# Revit family: Gleiter GL-100 m.Lasche, 2xAG
name_source: partatom
category: HLS-Bauteile
revit_build: Autodesk Revit 2017 (Build: 20190507_1515(x64)
units: mm (PartAtom-declared; Revit-internal decimal feet)

## family parameters
Arbeitsebenenbasiert = Ja
Beim Laden mit Abzugskörper schneiden = Nein
Bemaßung runder Anschluss = Durchmesser verwenden
Gemeinsam genutzt = Ja
Immer vertikal = Nein
Raumberechnungspunkt = Nein
Teiletyp = Normal

## types (4) — shared parameters
Anzahl Anschlüsse = 2
Ausführung = mit Lasche
B = 160 mm  [stored 0.524934 ft]
B1 = 50 mm  [stored 0.164042 ft]
Breite = 125 mm  [stored 0.410105 ft]
DVS = 14 mm  [stored 0.0459318 ft]
Fabrikat = MEFA
Firma = MEFA Befestigungs- und Montagesysteme GmbH
Gleitreibungsfaktor = 0.15 - 0.25
Haftreibungsfaktor = 0,2 - 0,3
Kurztext1 = Gleiter axial GL 100
L = 125 mm  [stored 0.410105 ft]
L1 = 96 mm  [stored 0.314961 ft]
Lochdurchmesser = 13 mm
Länge = 160 mm  [stored 0.524934 ft]
Material Gleitelement = Stahl
Material Gleitstreifen = Kunststoff
Materialname Gleitelement = S235JR
Materialname Gleitstreifen = Polyamid 6
Mengeneinheit = St
Vorgabe-Ansicht = 1219 mm
max. Schiebeweg axial = 75 mm
max. Temperaturbeständigkeit = 100 °C

## per-type parameters (varying)
| type | Anschluss | Artikelnummer | Bauhöhe | EAN | Gewicht | Gewicht pro Bauteil | Gewinde | Gl-100, 2xAG | H | Kurztext2 | vpe |
| Gleiter GL-100 m. Lasche, 2x M10 | 2 x M10 | 0770530 | 40 mm | 4250928417909 | 0.77 kg | 0.77 kg | M10 | Gleiter GL-100, 2xAG : Gleiter GL-100, 2x AG M10 | 40 mm  [stored 0.131234 ft] | Anschluss 2 x M10 mit Lasche | 20 St |
| Gleiter GL-100 m. Lasche, 2x M12 | 2 x M12 | 0770538 | 42 mm | 4250928417961 | 0.79 kg | 0.79 kg | M12 | Gleiter GL-100, 2xAG : Gleiter GL-100, 2x AG M12 | 42 mm  [stored 0.137795 ft] | Anschluss 2 x M12 mit Lasche | 20 St |
| Gleiter GL-100 m. Lasche, 2x M16 | 2 x M16 | 0770565 | 41 mm | 4250928418074 | 0.81 kg | 0.81 kg | M16 | Gleiter GL-100, 2xAG : Gleiter GL-100, 2x AG M16 | 41 mm  [stored 0.134514 ft] | Anschluss 2 x M16 mit Lasche | 1 St |
| Gleiter GL-100 m. Lasche, 2x 1/2" | 2 x 1/2'' | 0770611 | 41 mm | 4250928418142 | 0.79 kg | 0.79 kg | 1/2'' | Gleiter GL-100, 2xAG : Gleiter GL-100, 2x AG Muffe halbe Zoll | 41 mm  [stored 0.134514 ft] | Anschluss 2 x 1/2'' mit Lasche | 1 St |

note: [stored X ft] marks values corroborated as IEEE doubles in the binary element streams (Revit-internal decimal feet)

## geometry (parser evidence)
native form markers: Sweep x3
no freeform markers — native parametric forms only
